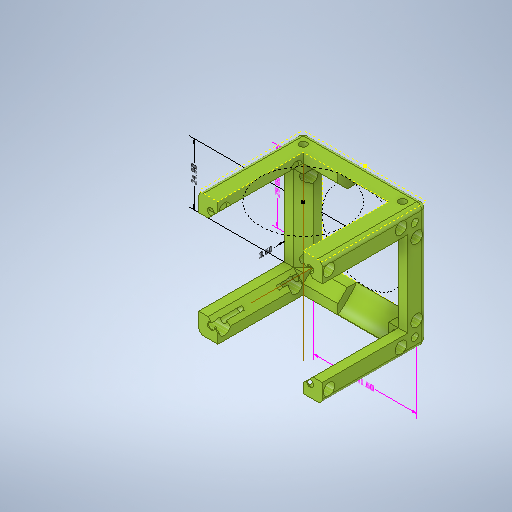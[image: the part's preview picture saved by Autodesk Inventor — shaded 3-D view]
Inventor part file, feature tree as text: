
AUTODESK INVENTOR PART (.ipt)
format: ipt  version: 2025.1 (Build 291241000, 241)  size: 707,584 bytes
history: native  units: mm
features: sketch x13, projected_geometry x9, hole x8, other x7, extrude x6, fillet x1, plane x1
ambient origin geometry x8: Origin, YZ Plane, XZ Plane, XY Plane, X Axis, Y Axis, Z Axis, Center Point
bodies: Solid1 (feature_tree)
feature tree (45):
  extrude  "Extrusion1"  Depth=49.8mm
  extrude  "Extrusion2"  Depth=7.7mm TaperAngle=0.0deg
  hole  "Hole1"  [1 undecoded]
  sketch  "Sketch4"  dims[d8=2.8mm d9=6.0mm d10=5.5mm d11=3.1mm d12=90.0deg d13=16.0mm d14=20.594885mm d23=2.0mm d30=33.8mm d31=0.0mm]
  sketch  "Sketch5"  dims[d35=33.8mm d36=0.0mm d37=54.2mm]
  other  "Work Axis1"
  other  "Work Axis2"
  fillet  "Fillet1"  Radius=33.8mm
  extrude  "Extrusion3"  Depth=54.2mm
  extrude  "Extrusion4"  Depth=54.2mm
  plane  "Work Plane1"
  extrude  "Extrusion5"  Depth=2.0mm
  hole  "Hole2"  [1 undecoded]
  hole  "Hole4"  [1 undecoded]
  hole  "Hole5"  [1 undecoded]
  hole  "Hole6"  [1 undecoded]
  hole  "Hole7"  [1 undecoded]
  hole  "Hole8"  [1 undecoded]
  hole  "孔9"  [1 undecoded]
  extrude  "拉伸6"  Depth=20.4mm
  sketch  "Sketch1"  dims[d0=49.8mm d1=49.8mm]
  sketch  "Sketch2"  dims[d2=7.7mm d3=7.7mm d4=0.0mm]
  projected_geometry  "Projected Loop1"
  sketch  "Sketch3"  dims[d5=34.4mm d6=0.0mm]
  projected_geometry  "Projected Loop3"
  projected_geometry  "Projected Loop4"
  projected_geometry  "Projected Loop5"
  projected_geometry  "Projected Loop6"
  projected_geometry  "Projected Loop7"
  sketch  "Sketch9"  dims[d38=135.0deg d39=54.2mm]
  sketch  "Sketch11"  dims[d40=33.8mm d41=0.0mm]
  projected_geometry  "Projected Loop11"
  sketch  "Sketch12"  dims[d42=2.8mm d43=6.0mm d44=3.0mm d45=2.0mm d46=90.0deg d47=12.0mm d48=20.594885mm]
  sketch  "Sketch13"  dims[d58=2.9mm d59=6.0mm d60=4.0mm d61=2.0mm d62=90.0deg d63=6.5mm d64=20.594885mm]
  sketch  "Sketch14"  dims[d67=2.9mm d68=6.0mm d69=4.0mm d70=2.0mm d71=90.0deg d72=6.5mm d73=20.594885mm]
  sketch  "Sketch15"  dims[d74=2.9mm d75=6.0mm d76=4.0mm d77=2.0mm d78=90.0deg d79=6.5mm d80=20.594885mm]
  projected_geometry  "Projected Loop13"
  projected_geometry  "Projected Loop14"
  sketch  "草图16"  dims[d81=2.9mm d82=6.0mm d83=4.0mm d84=2.0mm d85=90.0deg d86=6.5mm d87=20.594885mm d88=4.9mm]
  sketch  "草图17"  dims[d89=4.9mm d90=4.9mm d91=4.9mm d92=4.9mm d93=4.9mm d94=4.9mm d96=4.9mm d97=4.9mm d98=4.9mm d99=4.9mm d100=4.9mm d101=4.9mm d102=4.9mm d111=0.0mm d113=4.7mm d114=6.0mm d115=4.0mm d116=2.0mm d117=90.0deg d118=8.0mm d119=20.594885mm d120=54.2mm d121=54.2mm d122=54.0mm d123=54.0mm d126=41.6mm d127=29.0mm d128=41.6mm d129=29.0mm d130=4.7mm d131=6.0mm d132=4.0mm d133=2.0mm d134=90.0deg d135=8.0mm d136=20.594885mm d137=60.2mm d138=20.4mm d139=0.0mm d124=29.0mm d125=41.6mm d140=24.9mm d141=29.0mm d142=9.210439mm d143=3.6mm]
  other  "线性尺寸 1"
  other  "线性尺寸 2"
  other  "线性尺寸 3"
  other  "线性尺寸 4"
  other  "线性尺寸 5"
note: 8 required parameter values undecoded (feature->parameter linkage not recoverable at this tier; creation-order binding heuristic only, values carry confidence <= 0.55)
